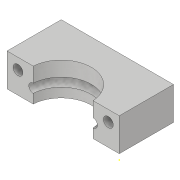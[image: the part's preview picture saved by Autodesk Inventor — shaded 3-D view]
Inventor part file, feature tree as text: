
AUTODESK INVENTOR PART (.ipt)
format: ipt  version: 2020 (Build 240168000, 168)  size: 200,704 bytes
history: native  units: in
note: dims shown in document units (in); Inventor stores cm internally (conversion verified against a paired STEP export)
features: sketch x16, extrude x9, sweep x3, plane x1, mirror x1
ambient origin geometry x8: Origin, YZ Plane, XZ Plane, XY Plane, X Axis, Y Axis, Z Axis, Center Point
bodies: Solid1 (feature_tree)
feature tree (30):
  extrude  "Extrusion1"  Depth=1.6142in
  extrude  "Extrusion2"  Depth=0.7874in
  extrude  "Extrusion3"  Depth=0.9252in
  extrude  "Extrusion4"  Depth=0.1772in TaperAngle=0.0deg
  extrude  "Extrusion5"  Depth=0.1417in
  extrude  "Extrusion6"  [1 undecoded]
  plane  "Work Plane1"
  mirror  "Mirror1"
  sweep  "Sweep1"
  sweep  "Sweep2"
  extrude  "Extrusion7"  Depth=0.8628in
  extrude  "Extrusion8"  Depth=0.126in
  extrude  "Extrusion9"  [1 undecoded]
  sketch  "Sketch18"
  sweep  "Sweep4"
  sketch  "Sketch1"  dims[d0=1.6142in d1=1.6142in]
  sketch  "Sketch3"  dims[d2=0.374in d3=0.0in d5=0.7874in]
  sketch  "Sketch4"  dims[d6=0.3937in d7=0.0in d8=0.9252in]
  sketch  "Sketch5"  dims[d9=0.1969in d10=0.0in d11=0.1772in d12=0.0in]
  sketch  "Sketch6"  dims[d13=0.8071in d14=0.0in d15=0.1417in]
  sketch  "Sketch8"  dims[d16=0.8071in d17=0.0in d18=-0.8071in]
  sketch  "Sketch9"  dims[d19=0.0in d20=0.0in d21=0.126in]
  sketch  "Sketch11"  dims[d22=0.0in d23=0.0in d24=0.0787in d25=0.0in]
  sketch  "Sketch12"  dims[d26=0.0276in d27=0.0in d28=0.8628in]
  sketch  "3D Sketch1"
  sketch  "Sketch13"  dims[d29=0.5906in d30=0.0in d34=0.126in]
  sketch  "Sketch14"  dims[d35=0.0in d36=0.0in]
  sketch  "Sketch15"
  sketch  "Sketch19"
  sketch  "Sketch20"
note: 2 required parameter values undecoded (feature->parameter linkage not recoverable at this tier; creation-order binding heuristic only, values carry confidence <= 0.55)
